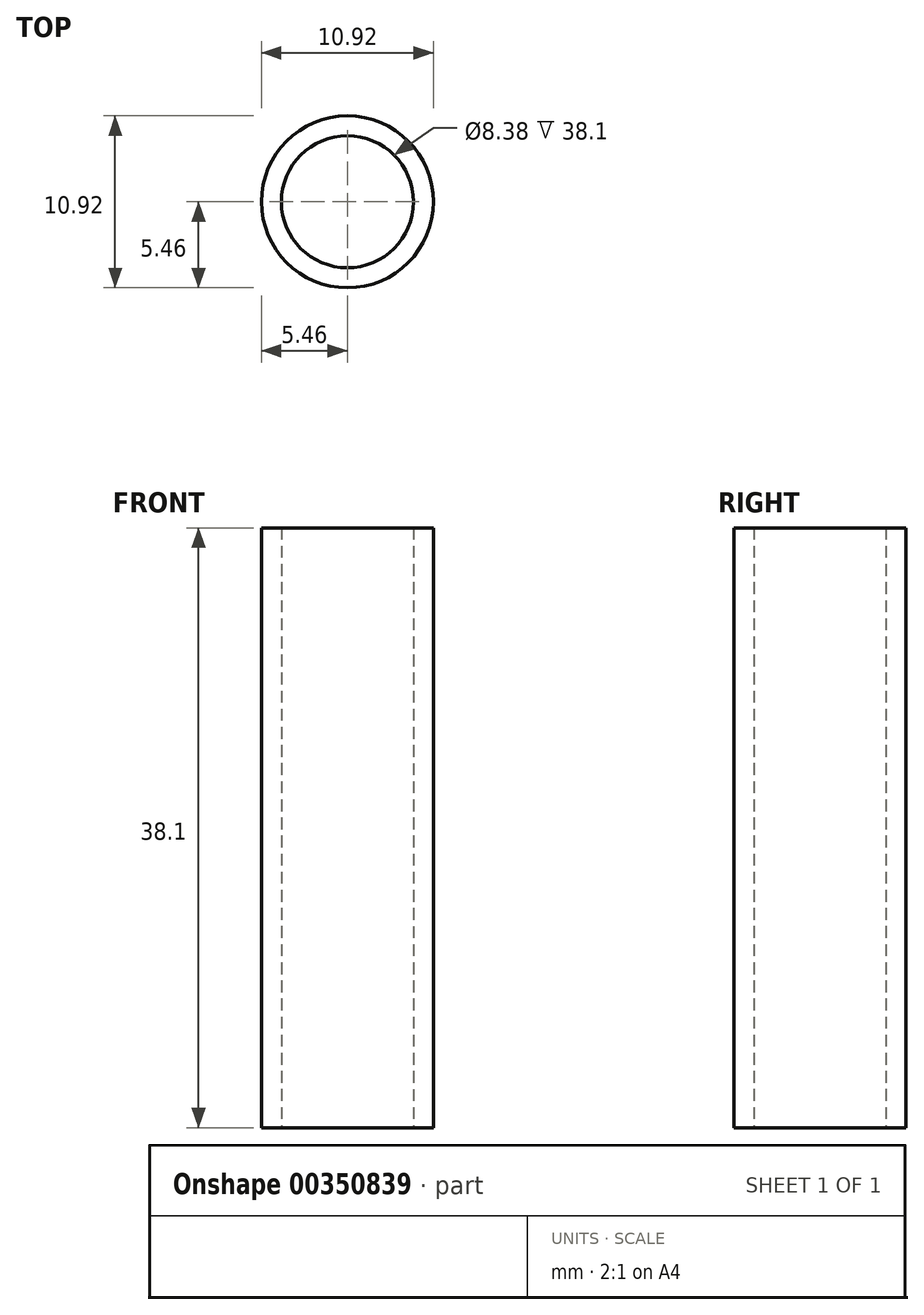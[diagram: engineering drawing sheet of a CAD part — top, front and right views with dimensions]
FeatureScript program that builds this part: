
annotation { "Feature Type Name" : "Feature", "Feature Type Description" : "" }
export const myFeature = defineFeature(function(context is Context, id is Id, definition is map)
    precondition{}
    {
        {
            var Q0;
            Q0=qCreatedBy(makeId("Top.planeOp"),FACE);
            var sketch = newSketch(context, id + "F0", { "sketchPlane" : qUnion([Q0])});
            skCircle(sketch, "E0", {"center": v(0, 0) * mm, "radius": 4.2 * mm});
            skCircle(sketch, "E1", {"center": v(0, 0) * mm, "radius": 5.46 * mm});
            skSolve(sketch);
        }
        {
            var Q0;
            Q0 = qSketchRegion(id + "F0", true);
            extrude(context, id + "F1", {"entities" : qUnion([Q0]), "depth" : 38.1 * mm});
        }
    });
